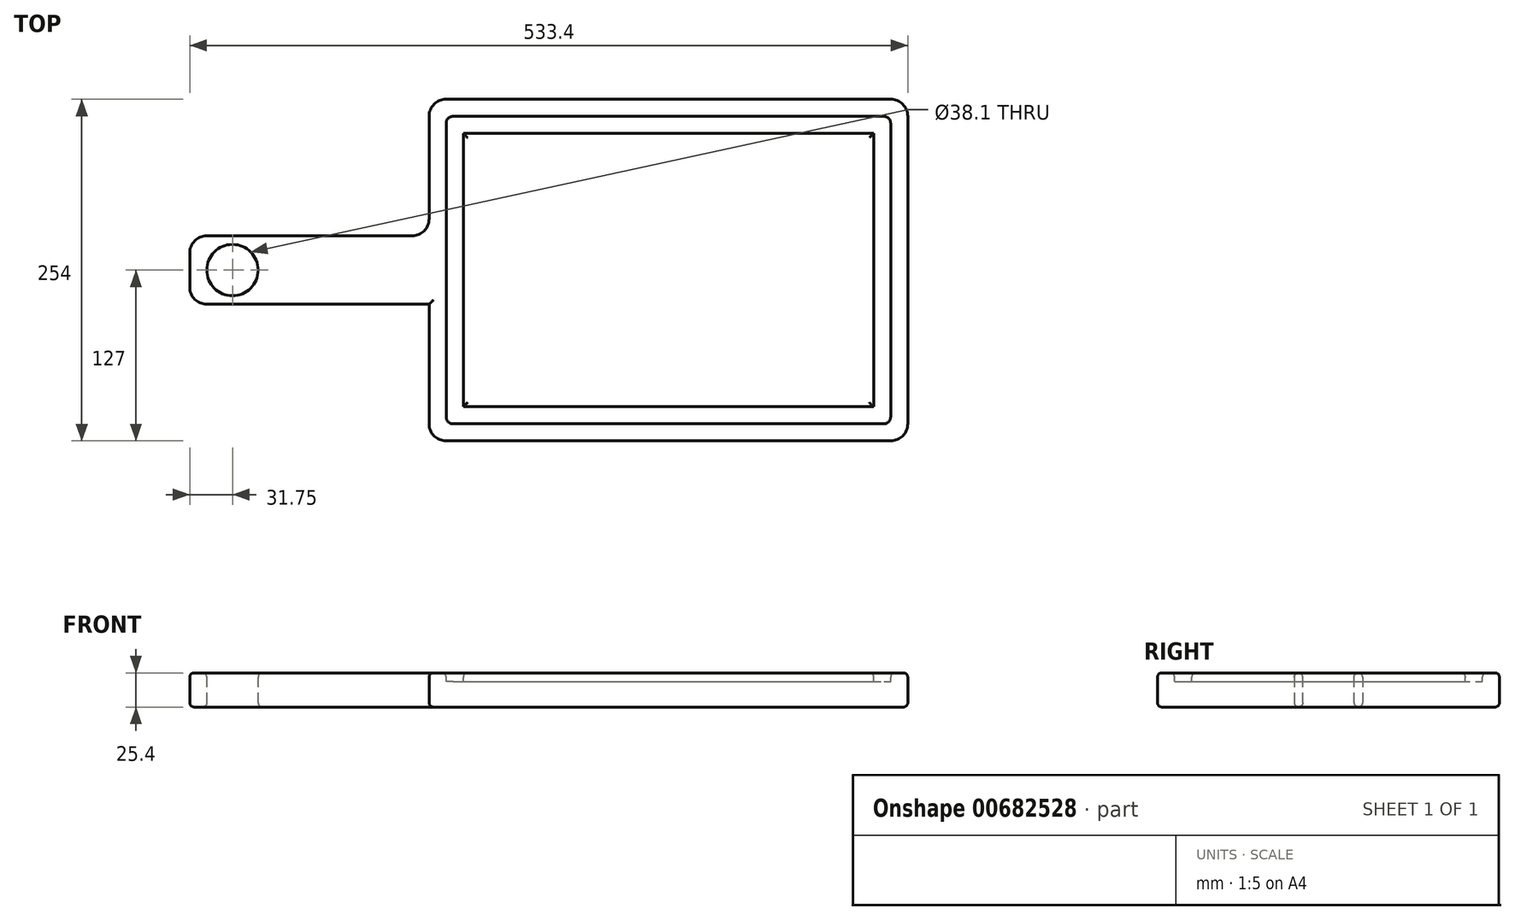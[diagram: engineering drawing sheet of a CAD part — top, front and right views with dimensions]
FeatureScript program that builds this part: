
annotation { "Feature Type Name" : "Feature", "Feature Type Description" : "" }
export const myFeature = defineFeature(function(context is Context, id is Id, definition is map)
    precondition{}
    {
        {
            var Q0;
            Q0=qCreatedBy(makeId("Top.planeOp"),FACE);
            var sketch = newSketch(context, id + "F0", { "sketchPlane" : qUnion([Q0])});
            skLineSegment(sketch, "E0.bottom", {"start": v(0, 0) * mm, "end": v(355.6, 0) * mm});
            skLineSegment(sketch, "E0.top", {"start": v(0, 254) * mm, "end": v(355.6, 254) * mm});
            skLineSegment(sketch, "E0.left", {"start": v(0, 0) * mm, "end": v(0, 254) * mm});
            skLineSegment(sketch, "E0.right", {"start": v(355.6, 0) * mm, "end": v(355.6, 254) * mm});
            skLineSegment(sketch, "E1.bottom", {"start": v(0, 152.4) * mm, "end": v(-177.8, 152.4) * mm});
            skLineSegment(sketch, "E1.top", {"start": v(0, 101.6) * mm, "end": v(-177.8, 101.6) * mm});
            skLineSegment(sketch, "E1.left", {"start": v(0, 152.4) * mm, "end": v(0, 101.6) * mm});
            skLineSegment(sketch, "E1.right", {"start": v(-177.8, 152.4) * mm, "end": v(-177.8, 101.6) * mm});
            skSolve(sketch);
        }
        {
            var Q0;
            {var subQ3=sQuery(id+"F0.wireOp",EDGE,"E0.bottom");Q0=makeQuery(id+"F0.imprint","IMPRINT",FACE,{"disambiguationData":[TD([[makeQuery(id+"F0.imprint","IMPRINT",EDGE,{"derivedFrom":subQ3}),1.0]])]});}
            var Q1;
            Q1=makeQuery(id+"F0.imprint","IMPRINT",FACE,{"disambiguationData":[TD([[makeQuery(id+"F0.imprint","IMPRINT",EDGE,{"derivedFrom":sQuery(id+"F0.wireOp",EDGE,"E1.bottom")}),1.0]])]});
            extrude(context, id + "F1", {"entities" : qUnion([Q0, Q1]), "depth" : 25.4 * mm, "offsetDistance" : 25.4 * mm});
        }
        {
            var Q0;
            Q0=makeQuery(id+"F1.opExtrude","CAP_FACE",FACE,{"disambiguationData":[OSD([sQuery(id+"F0.wireOp",EDGE,"E0.bottom"),sQuery(id+"F0.wireOp",EDGE,"E0.top"),sQuery(id+"F0.wireOp",EDGE,"E0.left"),sQuery(id+"F0.wireOp",EDGE,"E0.right"),sQuery(id+"F0.wireOp",EDGE,"E1.bottom"),sQuery(id+"F0.wireOp",EDGE,"E1.top"),sQuery(id+"F0.wireOp",EDGE,"E1.right")])],"isStart":false});
            var sketch = newSketch(context, id + "F2", { "sketchPlane" : qUnion([Q0])});
            skCircle(sketch, "E2", {"center": v(-146.05, 127) * mm, "radius": 19.05 * mm});
            skSolve(sketch);
        }
        {
            var Q0;
            Q0=makeQuery(id+"F2.imprint","IMPRINT",FACE,{"disambiguationData":[TD([[makeQuery(id+"F2.imprint","IMPRINT",EDGE,{"derivedFrom":sQuery(id+"F2.wireOp",EDGE,"E2")}),1.0]])]});
            extrude(context, id + "F3", {"entities" : qUnion([Q0]), "operationType" : NewBodyOperationType.REMOVE, "oppositeDirection" : true, "depth" : 25.4 * mm, "offsetDistance" : 25.4 * mm});
        }
        {
            var Q0;
            Q0=makeQuery(id+"F1.opExtrude","CAP_FACE",FACE,{"disambiguationData":[OSD([sQuery(id+"F0.wireOp",EDGE,"E0.bottom"),sQuery(id+"F0.wireOp",EDGE,"E0.top"),sQuery(id+"F0.wireOp",EDGE,"E0.left"),sQuery(id+"F0.wireOp",EDGE,"E0.right"),sQuery(id+"F0.wireOp",EDGE,"E1.bottom"),sQuery(id+"F0.wireOp",EDGE,"E1.top"),sQuery(id+"F0.wireOp",EDGE,"E1.right")])],"isStart":false});
            var sketch = newSketch(context, id + "F4", { "sketchPlane" : qUnion([Q0])});
            skLineSegment(sketch, "E3.0", {"start": v(12.7, 12.7) * mm, "end": v(12.7, 101.6) * mm});
            skLineSegment(sketch, "E3.1", {"start": v(12.7, 152.4) * mm, "end": v(12.7, 241.3) * mm});
            skLineSegment(sketch, "E3.2", {"start": v(12.7, 241.3) * mm, "end": v(342.9, 241.3) * mm});
            skLineSegment(sketch, "E3.3", {"start": v(342.9, 12.7) * mm, "end": v(342.9, 241.3) * mm});
            skLineSegment(sketch, "E3.4", {"start": v(12.7, 12.7) * mm, "end": v(342.9, 12.7) * mm});
            skLineSegment(sketch, "E4", {"start": v(12.7, 152.4) * mm, "end": v(12.7, 101.6) * mm});
            skLineSegment(sketch, "E5.0", {"start": v(25.4, 152.4) * mm, "end": v(25.4, 228.6) * mm});
            skLineSegment(sketch, "E5.1", {"start": v(330.2, 25.4) * mm, "end": v(330.2, 228.6) * mm});
            skLineSegment(sketch, "E5.2", {"start": v(25.4, 25.4) * mm, "end": v(330.2, 25.4) * mm});
            skLineSegment(sketch, "E5.3", {"start": v(25.4, 228.6) * mm, "end": v(330.2, 228.6) * mm});
            skLineSegment(sketch, "E5.4", {"start": v(25.4, 25.4) * mm, "end": v(25.4, 101.6) * mm});
            skLineSegment(sketch, "E5.5", {"start": v(25.4, 152.4) * mm, "end": v(25.4, 101.6) * mm});
            skLineSegment(sketch, "E6.0", {"start": v(355.6, 254) * mm, "end": v(0, 254) * mm});
            skLineSegment(sketch, "E6.1", {"start": v(355.6, 0) * mm, "end": v(355.6, 254) * mm});
            skLineSegment(sketch, "E6.2", {"start": v(0, 254) * mm, "end": v(0, 152.4) * mm});
            skLineSegment(sketch, "E6.3", {"start": v(0, 0) * mm, "end": v(355.6, 0) * mm});
            skLineSegment(sketch, "E6.4", {"start": v(0, 152.4) * mm, "end": v(-177.8, 152.4) * mm});
            skLineSegment(sketch, "E6.5", {"start": v(-177.8, 152.4) * mm, "end": v(-177.8, 101.6) * mm});
            skLineSegment(sketch, "E6.6", {"start": v(-177.8, 101.6) * mm, "end": v(0, 101.6) * mm});
            skLineSegment(sketch, "E6.7", {"start": v(0, 101.6) * mm, "end": v(0, 0) * mm});
            skSolve(sketch);
        }
        {
            var Q0;
            Q0=makeQuery(id+"F4.imprint","IMPRINT",FACE,{"disambiguationData":[TD([[makeQuery(id+"F4.imprint","IMPRINT",EDGE,{"derivedFrom":sQuery(id+"F4.wireOp",EDGE,"E3.0")}),-1.0]])]});
            extrude(context, id + "F5", {"entities" : qUnion([Q0]), "operationType" : NewBodyOperationType.REMOVE, "oppositeDirection" : true, "depth" : 6.35 * mm, "offsetDistance" : 25.4 * mm});
        }
        {
            var Q0;
            Q0=makeQuery(id+"F5.boolean.opBoolean","COPY",EDGE,{"derivedFrom":makeQuery(id+"F5.opExtrude","SWEPT_EDGE",EDGE,{"disambiguationData":[OSD([sQuery(id+"F4.wireOp",EDGE,"E3.1"),sQuery(id+"F4.wireOp",EDGE,"E3.2")])]})});
            var Q1;
            Q1=makeQuery(id+"F5.boolean.opBoolean","COPY",EDGE,{"derivedFrom":makeQuery(id+"F5.opExtrude","SWEPT_EDGE",EDGE,{"disambiguationData":[OSD([sQuery(id+"F4.wireOp",EDGE,"E3.2"),sQuery(id+"F4.wireOp",EDGE,"E3.3")])]})});
            var Q2;
            Q2=makeQuery(id+"F5.boolean.opBoolean","COPY",EDGE,{"derivedFrom":makeQuery(id+"F5.opExtrude","SWEPT_EDGE",EDGE,{"disambiguationData":[OSD([sQuery(id+"F4.wireOp",EDGE,"E3.0"),sQuery(id+"F4.wireOp",EDGE,"E3.4")])]})});
            var Q3;
            Q3=makeQuery(id+"F5.boolean.opBoolean","COPY",EDGE,{"derivedFrom":makeQuery(id+"F5.opExtrude","SWEPT_EDGE",EDGE,{"disambiguationData":[OSD([sQuery(id+"F4.wireOp",EDGE,"E3.3"),sQuery(id+"F4.wireOp",EDGE,"E3.4")])]})});
            fillet(context, id + "F6", {"entities" : qUnion([Q0, Q1, Q2, Q3]), "radius" : 5.08 * mm, "tangentPropagation" : true, "allowEdgeOverflow" : false});
        }
        {
            var Q0;
            Q0=makeQuery(id+"F1.opExtrude","SWEPT_EDGE",EDGE,{"disambiguationData":[OSD([sQuery(id+"F0.wireOp",EDGE,"E0.bottom"),sQuery(id+"F0.wireOp",EDGE,"E0.right")])]});
            var Q1;
            Q1=makeQuery(id+"F1.opExtrude","SWEPT_EDGE",EDGE,{"disambiguationData":[OSD([sQuery(id+"F0.wireOp",EDGE,"E0.bottom"),sQuery(id+"F0.wireOp",EDGE,"E0.left")])]});
            var Q2;
            Q2=makeQuery(id+"F1.opExtrude","SWEPT_EDGE",EDGE,{"disambiguationData":[OSD([sQuery(id+"F0.wireOp",EDGE,"E1.top"),sQuery(id+"F0.wireOp",EDGE,"E1.right")])]});
            var Q3;
            Q3=makeQuery(id+"F1.opExtrude","SWEPT_EDGE",EDGE,{"disambiguationData":[OSD([sQuery(id+"F0.wireOp",EDGE,"E1.bottom"),sQuery(id+"F0.wireOp",EDGE,"E1.right")])]});
            var Q4;
            Q4=makeQuery(id+"F1.opExtrude","SWEPT_EDGE",EDGE,{"disambiguationData":[OSD([sQuery(id+"F0.wireOp",EDGE,"E0.left"),sQuery(id+"F0.wireOp",EDGE,"E1.bottom"),sQuery(id+"F0.wireOp",EDGE,"E1.left")])]});
            var Q5;
            Q5=makeQuery(id+"F1.opExtrude","SWEPT_EDGE",EDGE,{"disambiguationData":[OSD([sQuery(id+"F0.wireOp",EDGE,"E0.top"),sQuery(id+"F0.wireOp",EDGE,"E0.left")])]});
            var Q6;
            Q6=makeQuery(id+"F1.opExtrude","SWEPT_EDGE",EDGE,{"disambiguationData":[OSD([sQuery(id+"F0.wireOp",EDGE,"E0.top"),sQuery(id+"F0.wireOp",EDGE,"E0.right")])]});
            fillet(context, id + "F7", {"entities" : qUnion([Q0, Q1, Q2, Q3, Q4, Q5, Q6]), "radius" : 12.7 * mm, "tangentPropagation" : true, "allowEdgeOverflow" : false});
        }
        {
            var Q0;
            Q0=makeQuery(id+"F5.boolean.opBoolean","SPLIT",FACE,{"disambiguationData":[TD([makeQuery(id+"F5.opExtrude","SWEPT_FACE",FACE,{"disambiguationData":[OSD([sQuery(id+"F4.wireOp",EDGE,"E5.1")])]})])],"derivedFrom":makeQuery(id+"F1.opExtrude","CAP_FACE",FACE,{"disambiguationData":[OSD([sQuery(id+"F0.wireOp",EDGE,"E0.bottom"),sQuery(id+"F0.wireOp",EDGE,"E0.top"),sQuery(id+"F0.wireOp",EDGE,"E0.left"),sQuery(id+"F0.wireOp",EDGE,"E0.right"),sQuery(id+"F0.wireOp",EDGE,"E1.bottom"),sQuery(id+"F0.wireOp",EDGE,"E1.top"),sQuery(id+"F0.wireOp",EDGE,"E1.right")])],"isStart":false})});
            var Q1;
            {var subQ0=sQuery(id+"F0.wireOp",EDGE,"E0.left");var subQ1=sQuery(id+"F0.wireOp",EDGE,"E0.top");var subQ3=sQuery(id+"F0.wireOp",EDGE,"E1.bottom");var subQ4=sQuery(id+"F0.wireOp",EDGE,"E1.right");var subQ5=sQuery(id+"F0.wireOp",EDGE,"E1.top");var subQ6=sQuery(id+"F0.wireOp",EDGE,"E0.right");var subQ7=sQuery(id+"F0.wireOp",EDGE,"E0.bottom");Q1=makeQuery(id+"F5.boolean.opBoolean","SPLIT",FACE,{"disambiguationData":[TD([makeQuery(id+"F1.opExtrude","SWEPT_FACE",FACE,{"disambiguationData":[OSD([subQ7])]})])],"derivedFrom":makeQuery(id+"F1.opExtrude","CAP_FACE",FACE,{"disambiguationData":[OSD([subQ7,subQ1,subQ0,subQ6,subQ3,subQ5,subQ4])],"isStart":false})});}
            var Q2;
            Q2=makeQuery(id+"F1.opExtrude","CAP_FACE",FACE,{"disambiguationData":[OSD([sQuery(id+"F0.wireOp",EDGE,"E0.bottom"),sQuery(id+"F0.wireOp",EDGE,"E0.top"),sQuery(id+"F0.wireOp",EDGE,"E0.left"),sQuery(id+"F0.wireOp",EDGE,"E0.right"),sQuery(id+"F0.wireOp",EDGE,"E1.bottom"),sQuery(id+"F0.wireOp",EDGE,"E1.top"),sQuery(id+"F0.wireOp",EDGE,"E1.right")])],"isStart":true});
            fillet(context, id + "F8", {"entities" : qUnion([Q0, Q1, Q2]), "radius" : 3.17 * mm, "tangentPropagation" : true, "allowEdgeOverflow" : false});
        }
    });
